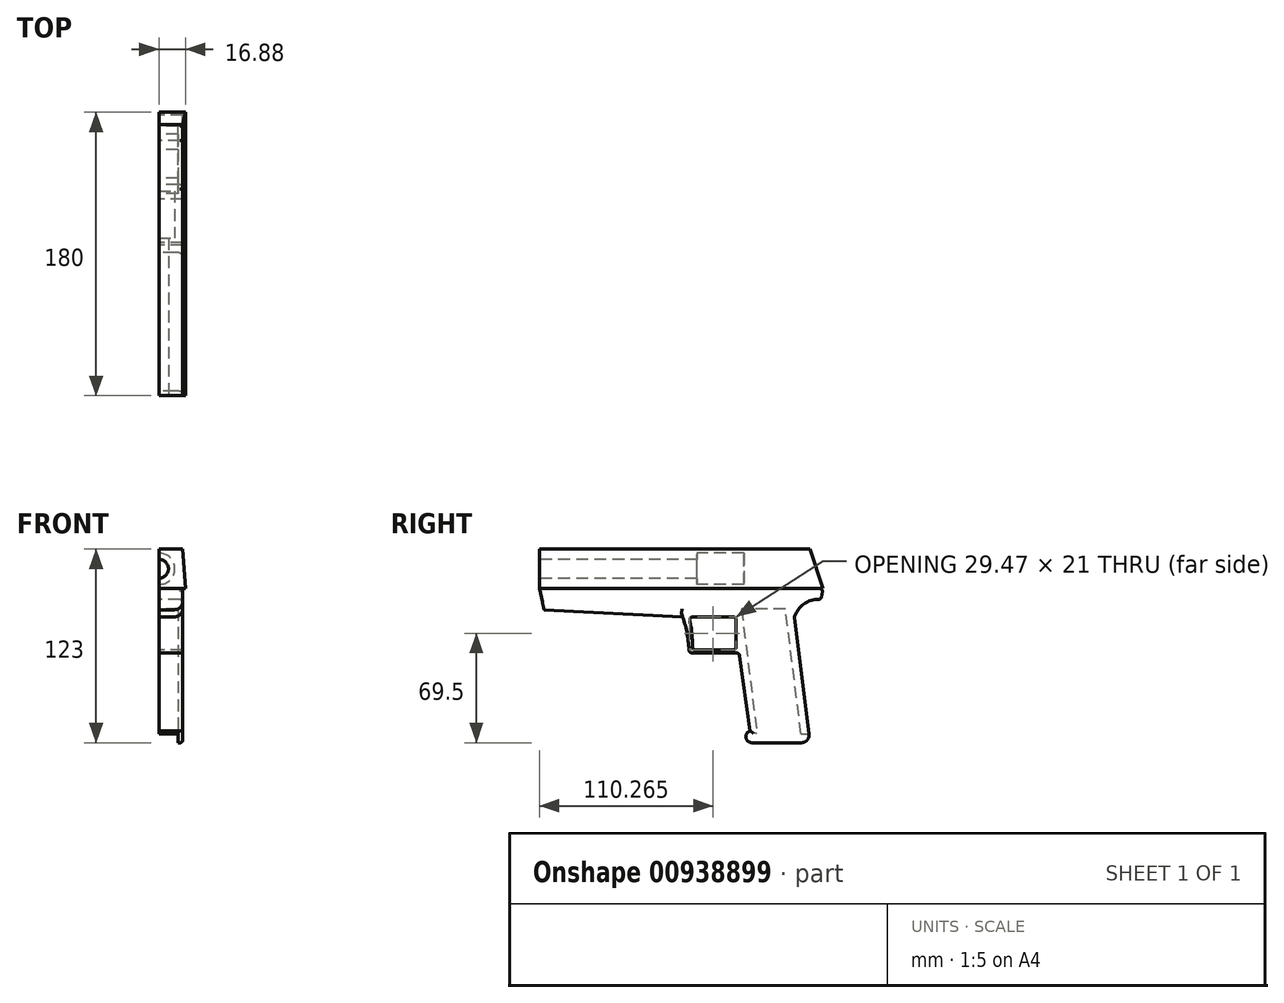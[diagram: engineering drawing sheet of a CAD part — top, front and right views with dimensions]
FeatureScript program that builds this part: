
annotation { "Feature Type Name" : "Feature", "Feature Type Description" : "" }
export const myFeature = defineFeature(function(context is Context, id is Id, definition is map)
    precondition{}
    {
        {
            var Q0;
            Q0=qCreatedBy(makeId("Right.planeOp"),FACE);
            var sketch = newSketch(context, id + "F0", { "sketchPlane" : qUnion([Q0])});
            skLineSegment(sketch, "E0.bottom", {"start": v(0, 0) * mm, "end": v(30, 0) * mm});
            skLineSegment(sketch, "E0.top", {"start": v(1.97, -23) * mm, "end": v(30, -23) * mm});
            skLineSegment(sketch, "E0.left", {"start": v(0, 0) * mm, "end": v(0, -23) * mm, "construction": true});
            skLineSegment(sketch, "E0.right", {"start": v(30, 0) * mm, "end": v(30, -23) * mm});
            skLineSegment(sketch, "E1.bottom", {"start": v(0, 0) * mm, "end": v(-91, 0) * mm});
            skLineSegment(sketch, "E1.top", {"start": v(0, 18) * mm, "end": v(-95, 18) * mm});
            skLineSegment(sketch, "E1.left", {"start": v(0, 0) * mm, "end": v(0, 18) * mm});
            skLineSegment(sketch, "E1.right", {"start": v(-95, 0) * mm, "end": v(-95, 18) * mm, "construction": true});
            skLineSegment(sketch, "E2", {"start": v(-95, 18) * mm, "end": v(-91, 0) * mm});
            skLineSegment(sketch, "E3", {"start": v(-95, 18) * mm, "end": v(-83, 0) * mm});
            skLineSegment(sketch, "E4", {"start": v(-95, 0) * mm, "end": v(-91, 0) * mm, "construction": true});
            skLineSegment(sketch, "E5.bottom", {"start": v(-95, 18) * mm, "end": v(85, 18) * mm});
            skLineSegment(sketch, "E5.top", {"start": v(-95, 43) * mm, "end": v(77, 43) * mm});
            skLineSegment(sketch, "E5.left", {"start": v(-95, 18) * mm, "end": v(-95, 43) * mm});
            skLineSegment(sketch, "E5.right", {"start": v(85, 18) * mm, "end": v(85, 43) * mm, "construction": true});
            skLineSegment(sketch, "E6", {"start": v(85, 18) * mm, "end": v(77, 43) * mm});
            skLineSegment(sketch, "E7", {"start": v(77, 43) * mm, "end": v(85, 43) * mm, "construction": true});
            skLineSegment(sketch, "E8.bottom", {"start": v(0, 18) * mm, "end": v(70, 18) * mm});
            skLineSegment(sketch, "E8.top", {"start": v(0, 0) * mm, "end": v(67, 0) * mm});
            skLineSegment(sketch, "E8.left", {"start": v(0, 18) * mm, "end": v(0, 0) * mm});
            skLineSegment(sketch, "E8.right", {"start": v(70, 18) * mm, "end": v(70, 5.34) * mm});
            skLineSegment(sketch, "E9.bottom", {"start": v(30, 0) * mm, "end": v(67, 0) * mm});
            skLineSegment(sketch, "E9.top", {"start": v(40, -80) * mm, "end": v(71.34, -80) * mm});
            skLineSegment(sketch, "E9.left", {"start": v(30, 0) * mm, "end": v(30, -80) * mm, "construction": true});
            skLineSegment(sketch, "E9.right", {"start": v(77, 0) * mm, "end": v(77, -80) * mm, "construction": true});
            skLineSegment(sketch, "E10", {"start": v(32.23, -24.72) * mm, "end": v(40, -80) * mm});
            skLineSegment(sketch, "E11", {"start": v(30, -80) * mm, "end": v(40, -80) * mm, "construction": true});
            skLineSegment(sketch, "E12", {"start": v(76.3, -74.38) * mm, "end": v(67, 0) * mm});
            skLineSegment(sketch, "E13", {"start": v(30, -23) * mm, "end": v(30.25, -23) * mm});
            skArc(sketch, "E14", {"start": v(-0.03, -21.06) * mm, "mid": v(-1.18, -10.37) * mm, "end": v(-4, 0) * mm});
            skPoint(sketch, "E15.visualSharp", {"position": v(0, -23) * mm});
            skArc(sketch, "E15.filletArc", {"start": v(-0.03, -21.06) * mm, "mid": v(0.58, -22.43) * mm, "end": v(1.97, -23) * mm});
            skArc(sketch, "E16.filletArc", {"start": v(32.23, -24.72) * mm, "mid": v(31.56, -23.5) * mm, "end": v(30.25, -23) * mm});
            skLineSegment(sketch, "E17", {"start": v(32.23, -24.72) * mm, "end": v(30, 0) * mm, "construction": true});
            skLineSegment(sketch, "E18", {"start": v(85, 18) * mm, "end": v(83.8, 11) * mm});
            skArc(sketch, "E19", {"start": v(83.8, 11) * mm, "mid": v(73.48, 8.42) * mm, "end": v(67, 0) * mm});
            skPoint(sketch, "E20.orphan", {"position": v(70, 0) * mm});
            skLineSegment(sketch, "E21", {"start": v(67, 0) * mm, "end": v(70, 0) * mm, "construction": true});
            skLineSegment(sketch, "E22", {"start": v(70, 5.34) * mm, "end": v(70, 0) * mm, "construction": true});
            skArc(sketch, "E23", {"start": v(1.97, -23) * mm, "mid": v(1.94, -11.42) * mm, "end": v(0, 0) * mm});
            skLineSegment(sketch, "E24", {"start": v(2.1, -21) * mm, "end": v(30, -21) * mm});
            skLineSegment(sketch, "E25", {"start": v(30, -21) * mm, "end": v(30, 0) * mm});
            skLineSegment(sketch, "E26.bottom", {"start": v(-25, 43) * mm, "end": v(10, 43) * mm});
            skLineSegment(sketch, "E26.top", {"start": v(-25, 29) * mm, "end": v(10, 29) * mm});
            skLineSegment(sketch, "E26.left", {"start": v(-25, 43) * mm, "end": v(-25, 29) * mm});
            skLineSegment(sketch, "E26.right", {"start": v(10, 43) * mm, "end": v(10, 29) * mm});
            skLineSegment(sketch, "E27", {"start": v(-92, 4.5) * mm, "end": v(-4, 0) * mm});
            skArc(sketch, "E28", {"start": v(38.94, -72.45) * mm, "mid": v(36.19, -76.68) * mm, "end": v(40, -80) * mm});
            skPoint(sketch, "E29.visualSharp", {"position": v(77, -80) * mm});
            skArc(sketch, "E29.filletArc", {"start": v(71.34, -80) * mm, "mid": v(75.08, -78.3) * mm, "end": v(76.3, -74.38) * mm});
            skSolve(sketch);
        }
        {
            var Q0;
            {var subQ0=sQuery(id+"F0.wireOp",EDGE,"E3");var subQ3=sQuery(id+"F0.wireOp",EDGE,"E27");var subQ5=makeQuery(id+"F0.imprint","INTERSECT",VERTEX,{"derivedFrom":[subQ0,subQ3]});Q0=makeQuery(id+"F0.imprint","IMPRINT",FACE,{"disambiguationData":[TD([[makeQuery(id+"F0.imprint","IMPRINT",EDGE,{"disambiguationData":[TD([[subQ5,1.0]])],"derivedFrom":subQ3}),1.0]])]});}
            var Q1;
            Q1=makeQuery(id+"F0.imprint","IMPRINT",FACE,{"disambiguationData":[TD([[makeQuery(id+"F0.imprint","IMPRINT",EDGE,{"derivedFrom":sQuery(id+"F0.wireOp",EDGE,"E0.bottom")}),1.0]])]});
            var Q2;
            {var subQ2=sQuery(id+"F0.wireOp",EDGE,"E8.right");Q2=makeQuery(id+"F0.imprint","IMPRINT",FACE,{"disambiguationData":[TD([[makeQuery(id+"F0.imprint","IMPRINT",EDGE,{"derivedFrom":subQ2}),1.0]])]});}
            var Q3;
            {var subQ0=sQuery(id+"F0.wireOp",EDGE,"E8.top");Q3=makeQuery(id+"F0.imprint","IMPRINT",FACE,{"disambiguationData":[TD([[makeQuery(id+"F0.imprint","IMPRINT",EDGE,{"derivedFrom":subQ0}),-1.0]])]});}
            var Q4;
            Q4=makeQuery(id+"F0.imprint","IMPRINT",FACE,{"disambiguationData":[TD([[makeQuery(id+"F0.imprint","IMPRINT",EDGE,{"derivedFrom":sQuery(id+"F0.wireOp",EDGE,"xTuj0VVL-X9Mf-9LgS-BpCr-QhpTMYPl40Ub.bottom")}),-1.0]])]});
            var Q5;
            {var subQ5=sQuery(id+"F0.wireOp",EDGE,"E14");Q5=makeQuery(id+"F0.imprint","IMPRINT",FACE,{"disambiguationData":[TD([[makeQuery(id+"F0.imprint","IMPRINT",EDGE,{"derivedFrom":subQ5}),-1.0]])]});}
            var Q6;
            {var subQ0=sQuery(id+"F0.wireOp",EDGE,"E0.top");Q6=makeQuery(id+"F0.imprint","IMPRINT",FACE,{"disambiguationData":[TD([[makeQuery(id+"F0.imprint","IMPRINT",EDGE,{"derivedFrom":subQ0}),1.0]])]});}
            var Q7;
            {var subQ1=sQuery(id+"F0.wireOp",EDGE,"E1.top");Q7=makeQuery(id+"F0.imprint","IMPRINT",FACE,{"disambiguationData":[TD([[makeQuery(id+"F0.imprint","IMPRINT",EDGE,{"derivedFrom":subQ1}),1.0]])]});}
            var Q8;
            {var subQ0=sQuery(id+"F0.wireOp",EDGE,"E28");Q8=makeQuery(id+"F0.imprint","IMPRINT",FACE,{"disambiguationData":[TD([[makeQuery(id+"F0.imprint","IMPRINT",EDGE,{"derivedFrom":subQ0}),1.0]])]});}
            extrude(context, id + "F1", {"entities" : qUnion([Q0, Q1, Q2, Q3, Q4, Q5, Q6, Q7, Q8]), "depth" : 15 * mm, "offsetDistance" : 25 * mm});
        }
        {
            var Q0;
            Q0=makeQuery(id+"F1.opExtrude","CAP_EDGE",EDGE,{"disambiguationData":[OSD([sQuery(id+"F0.wireOp",EDGE,"E12")])],"isStart":false});
            var Q1;
            Q1=makeQuery(id+"F1.opExtrude","CAP_EDGE",EDGE,{"disambiguationData":[OSD([sQuery(id+"F0.wireOp",EDGE,"E10")])],"isStart":false});
            var Q2;
            Q2=makeQuery(id+"F1.opExtrude","CAP_EDGE",EDGE,{"disambiguationData":[OSD([sQuery(id+"F0.wireOp",EDGE,"E9.top")])],"isStart":false});
            var Q3;
            Q3=makeQuery(id+"F1.opExtrude","SWEPT_EDGE",EDGE,{"disambiguationData":[OSD([sQuery(id+"F0.wireOp",EDGE,"E9.top"),sQuery(id+"F0.wireOp",EDGE,"E10"),sQuery(id+"F0.wireOp",EDGE,"E28")])]});
            var Q4;
            {var subQ0=sQuery(id+"F0.wireOp",EDGE,"E29.filletArc");Q4=qUnion([makeQuery(id+"F1.opExtrude","SWEPT_EDGE",EDGE,{"disambiguationData":[OSD([sQuery(id+"F0.wireOp",EDGE,"E9.top"),subQ0])]}),makeQuery(id+"F1.opExtrude","SWEPT_EDGE",EDGE,{"disambiguationData":[OSD([sQuery(id+"F0.wireOp",EDGE,"E12"),subQ0])]})]);}
            var Q5;
            Q5=makeQuery(id+"F1.opExtrude","CAP_EDGE",EDGE,{"disambiguationData":[OSD([sQuery(id+"F0.wireOp",EDGE,"E19")])],"isStart":false});
            var Q6;
            Q6=makeQuery(id+"F1.opExtrude","CAP_EDGE",EDGE,{"disambiguationData":[OSD([sQuery(id+"F0.wireOp",EDGE,"E18")])],"isStart":false});
            var Q7;
            Q7=makeQuery(id+"F1.opExtrude","CAP_EDGE",EDGE,{"disambiguationData":[OSD([sQuery(id+"F0.wireOp",EDGE,"E6")])],"isStart":false});
            var Q8;
            Q8=makeQuery(id+"F1.opExtrude","SWEPT_EDGE",EDGE,{"disambiguationData":[OSD([sQuery(id+"F0.wireOp",EDGE,"E5.bottom"),sQuery(id+"F0.wireOp",EDGE,"E6"),sQuery(id+"F0.wireOp",EDGE,"E18")])]});
            var Q9;
            Q9=makeQuery(id+"F1.opExtrude","SWEPT_EDGE",EDGE,{"disambiguationData":[OSD([sQuery(id+"F0.wireOp",EDGE,"E18"),sQuery(id+"F0.wireOp",EDGE,"E19")])]});
            var Q10;
            Q10=makeQuery(id+"F1.opExtrude","SWEPT_EDGE",EDGE,{"disambiguationData":[OSD([sQuery(id+"F0.wireOp",EDGE,"E8.top"),sQuery(id+"F0.wireOp",EDGE,"E12"),sQuery(id+"F0.wireOp",EDGE,"E19")])]});
            fillet(context, id + "F2", {"entities" : qUnion([Q0, Q1, Q2, Q3, Q4, Q5, Q6, Q7, Q8, Q9, Q10]), "radius" : 1.57 * mm, "tangentPropagation" : true, "allowEdgeOverflow" : false});
        }
        {
            var Q0;
            Q0=makeQuery(id+"F1.opExtrude","SWEPT_EDGE",EDGE,{"disambiguationData":[OSD([sQuery(id+"F0.wireOp",EDGE,"E23"),sQuery(id+"F0.wireOp",EDGE,"E24")])]});
            var Q1;
            Q1=makeQuery(id+"F1.opExtrude","SWEPT_EDGE",EDGE,{"disambiguationData":[OSD([sQuery(id+"F0.wireOp",EDGE,"E0.bottom"),sQuery(id+"F0.wireOp",EDGE,"E1.bottom"),sQuery(id+"F0.wireOp",EDGE,"E1.left"),sQuery(id+"F0.wireOp",EDGE,"E23")])]});
            var Q2;
            Q2=makeQuery(id+"F1.opExtrude","SWEPT_EDGE",EDGE,{"disambiguationData":[OSD([sQuery(id+"F0.wireOp",EDGE,"E0.right"),sQuery(id+"F0.wireOp",EDGE,"E24")])]});
            var Q3;
            Q3=makeQuery(id+"F1.opExtrude","SWEPT_EDGE",EDGE,{"disambiguationData":[OSD([sQuery(id+"F0.wireOp",EDGE,"E0.bottom"),sQuery(id+"F0.wireOp",EDGE,"E0.right"),sQuery(id+"F0.wireOp",EDGE,"E8.top")])]});
            fillet(context, id + "F3", {"entities" : qUnion([Q0, Q1, Q2, Q3]), "radius" : 2 * mm, "tangentPropagation" : true, "allowEdgeOverflow" : false});
        }
        {
            var Q0;
            Q0=makeQuery(id+"F1.opExtrude","CAP_EDGE",EDGE,{"disambiguationData":[OSD([sQuery(id+"F0.wireOp",EDGE,"E27")])],"isStart":false});
            var Q1;
            Q1=makeQuery(id+"FmSBhCIFCrbXICr_1.opPattern","COPY",EDGE,{"derivedFrom":makeQuery(id+"F1.opExtrude","CAP_EDGE",EDGE,{"disambiguationData":[OSD([sQuery(id+"F0.wireOp",EDGE,"E27")])],"isStart":false}),"instanceName":"1"});
            fillet(context, id + "F4", {"entities" : qUnion([Q0, Q1]), "radius" : 5 * mm, "tangentPropagation" : true, "allowEdgeOverflow" : false});
        }
        {
            var Q0;
            {var subQ6=sQuery(id+"F0.wireOp",EDGE,"E1.top");Q0=makeQuery(id+"F0.imprint","IMPRINT",FACE,{"disambiguationData":[TD([[makeQuery(id+"F0.imprint","IMPRINT",EDGE,{"derivedFrom":subQ6}),-1.0]])]});}
            var Q1;
            Q1=makeQuery(id+"F0.imprint","IMPRINT",FACE,{"disambiguationData":[TD([[makeQuery(id+"F0.imprint","IMPRINT",EDGE,{"derivedFrom":sQuery(id+"F0.wireOp",EDGE,"E26.top")}),1.0]])]});
            extrude(context, id + "F5", {"entities" : qUnion([Q0, Q1]), "operationType" : NewBodyOperationType.ADD, "depth" : 18 * mm, "offsetDistance" : 25 * mm});
        }
        {
            var Q0;
            Q0=makeQuery(id+"F5.opExtrude","CAP_EDGE",EDGE,{"disambiguationData":[OSD([sQuery(id+"F0.wireOp",EDGE,"E5.top")])],"isStart":false});
            chamfer(context, id + "F6", {"entities" : qUnion([Q0]), "chamferType" : ChamferType.TWO_OFFSETS, "width1" : 3 * mm, "oppositeDirection" : false, "width2" : 40 * mm, "tangentPropagation" : true});
        }
        {
            var Q0;
            Q0=makeQuery(id+"F5.opExtrude","SWEPT_FACE",FACE,{"disambiguationData":[OSD([sQuery(id+"F0.wireOp",EDGE,"E5.left")])]});
            var sketch = newSketch(context, id + "F7", { "sketchPlane" : qUnion([Q0])});
            skCircle(sketch, "E30", {"center": v(0, 30.5) * mm, "radius": 6 * mm});
            skSolve(sketch);
        }
        {
            var Q0;
            {var subQ0=sQuery(id+"F7.wireOp",EDGE,"E30");var subQ1=makeQuery(id+"F5.opExtrude","CAP_EDGE",EDGE,{"disambiguationData":[OSD([sQuery(id+"F0.wireOp",EDGE,"E5.left")])],"isStart":true});var subQ2=makeQuery(id+"F7.imprint","INTERSECT",VERTEX,{"disambiguationData":[OD(0.0)],"derivedFrom":[subQ1,subQ0]});Q0=makeQuery(id+"F7.imprint","IMPRINT",FACE,{"disambiguationData":[TD([[makeQuery(id+"F7.imprint","IMPRINT",EDGE,{"disambiguationData":[TD([[subQ2,1.0]])],"derivedFrom":subQ0}),1.0]])]});}
            extrude(context, id + "F8", {"entities" : qUnion([Q0]), "operationType" : NewBodyOperationType.REMOVE, "oppositeDirection" : true, "depth" : 100 * mm, "offsetDistance" : 25 * mm});
        }
        {
            var Q0;
            Q0=makeQuery(id+"F8.boolean.opBoolean","COPY",FACE,{"derivedFrom":makeQuery(id+"F8.opExtrude","CAP_FACE",FACE,{"disambiguationData":[OSD([sQuery(id+"F0.wireOp",EDGE,"E5.left"),sQuery(id+"F7.wireOp",EDGE,"E30")])],"isStart":false})});
            var sketch = newSketch(context, id + "F9", { "sketchPlane" : qUnion([Q0])});
            skCircle(sketch, "E31", {"center": v(0, 30.5) * mm, "radius": 10 * mm});
            skSolve(sketch);
        }
        {
            var Q0;
            Q0=makeQuery(id+"F9.imprint","IMPRINT",FACE,{"disambiguationData":[TD([[makeQuery(id+"F9.imprint","IMPRINT",EDGE,{"derivedFrom":sQuery(id+"F9.wireOp",EDGE,"E31")}),1.0]])]});
            var Q1;
            Q1=makeQuery(id+"F9.imprint","IMPRINT",FACE,{"disambiguationData":[TD([[makeQuery(id+"F9.imprint","IMPRINT",EDGE,{"derivedFrom":makeQuery(id+"F8.boolean.opBoolean","COPY",EDGE,{"derivedFrom":makeQuery(id+"F8.opExtrude","CAP_EDGE",EDGE,{"disambiguationData":[OSD([sQuery(id+"F7.wireOp",EDGE,"E30")])],"isStart":false})})}),1.0]])]});
            extrude(context, id + "F10", {"entities" : qUnion([Q0, Q1]), "operationType" : NewBodyOperationType.REMOVE, "oppositeDirection" : true, "depth" : 30 * mm, "offsetDistance" : 25 * mm});
        }
        {
            var Q0;
            {var subQ0=sQuery(id+"F0.wireOp",EDGE,"E5.bottom");var subQ1=sQuery(id+"F0.wireOp",EDGE,"E1.top");Q0=makeQuery(id+"F5.boolean.opBoolean","MERGE",FACE,{"derivedFrom":[makeQuery(id+"F1.opExtrude","CAP_FACE",FACE,{"disambiguationData":[OSD([sQuery(id+"F0.wireOp",EDGE,"E0.bottom"),sQuery(id+"F0.wireOp",EDGE,"E0.top"),sQuery(id+"F0.wireOp",EDGE,"E0.right"),subQ1,sQuery(id+"F0.wireOp",EDGE,"E2"),subQ0,sQuery(id+"F0.wireOp",EDGE,"E9.top"),sQuery(id+"F0.wireOp",EDGE,"E10"),sQuery(id+"F0.wireOp",EDGE,"E12"),sQuery(id+"F0.wireOp",EDGE,"E13"),sQuery(id+"F0.wireOp",EDGE,"E14"),sQuery(id+"F0.wireOp",EDGE,"E15.filletArc"),sQuery(id+"F0.wireOp",EDGE,"E16.filletArc"),sQuery(id+"F0.wireOp",EDGE,"E18"),sQuery(id+"F0.wireOp",EDGE,"E19"),sQuery(id+"F0.wireOp",EDGE,"E23"),sQuery(id+"F0.wireOp",EDGE,"E24"),sQuery(id+"F0.wireOp",EDGE,"E27"),sQuery(id+"F0.wireOp",EDGE,"E28"),sQuery(id+"F0.wireOp",EDGE,"E29.filletArc")])],"isStart":true}),makeQuery(id+"F5.opExtrude","CAP_FACE",FACE,{"disambiguationData":[OSD([subQ1,subQ0,sQuery(id+"F0.wireOp",EDGE,"E5.top"),sQuery(id+"F0.wireOp",EDGE,"E5.left"),sQuery(id+"F0.wireOp",EDGE,"E6")])],"isStart":true})]});}
            var sketch = newSketch(context, id + "F11", { "sketchPlane" : qUnion([Q0])});
            skLineSegment(sketch, "E32", {"start": v(-71.26, -74.38) * mm, "end": v(-61.34, 5) * mm});
            skLineSegment(sketch, "E33", {"start": v(-61.34, 5) * mm, "end": v(-33.34, 5) * mm});
            skLineSegment(sketch, "E34", {"start": v(-33.34, 5) * mm, "end": v(-43.26, -74.38) * mm});
            skLineSegment(sketch, "E35", {"start": v(-43.26, -74.38) * mm, "end": v(-71.26, -74.38) * mm});
            skLineSegment(sketch, "E36", {"start": v(-71.26, -74.38) * mm, "end": v(-76.3, -74.38) * mm});
            skLineSegment(sketch, "E37", {"start": v(-43.26, -74.38) * mm, "end": v(-38.94, -72.45) * mm});
            skArc(sketch, "E38.0", {"start": v(-71.34, -80) * mm, "mid": v(-75.08, -78.3) * mm, "end": v(-76.3, -74.38) * mm});
            skLineSegment(sketch, "E39.0", {"start": v(-40, -80) * mm, "end": v(-71.34, -80) * mm});
            skArc(sketch, "E40.0", {"start": v(-38.94, -72.45) * mm, "mid": v(-36.19, -76.68) * mm, "end": v(-40, -80) * mm});
            skSolve(sketch);
        }
        {
            var Q0;
            Q0 = qSketchRegion(id + "F11", true);
            extrude(context, id + "F12", {"entities" : qUnion([Q0]), "operationType" : NewBodyOperationType.REMOVE, "oppositeDirection" : true, "depth" : 12 * mm, "offsetDistance" : 25 * mm});
        }
    });
